# Revit family: Haworth_BuzziNordic_ST100_LoungeChair
name_source: partatom
category: Furniture
revit_build: Autodesk Revit 2018 (Build: 20170223_1515(x64)
units: mm (PartAtom-declared; Revit-internal decimal feet)

## family parameters
Always vertical = Yes
Cut with Voids When Loaded = No
Room Calculation Point = No
Shared = No
Work Plane-Based = No

## types (2) — shared parameters
Actual Depth = 30.71 "
Actual Height = 31.89 "
Assembly Code = E2020200
Manufacturer = Haworth
Model = HCBZ-N1L1
Note = Verify Final Dim. w/ Haworth
Revision = 1
Seat Height = 16.54 "
URL = http://www.haworth.com
URL - Product = https://www.haworth.com
Warranty = http://www.haworth.com

## per-type parameters (varying)
| type | Actual Width | Back Support Width | Description | Seat Width | Spindle Offset | Wide |
| HCBZ-N1L1 - Lounge Chair | 28.15 " | 23.4 " | Haworth BuzziNordic Lounge Chair | 22.05 " | 3.9 " | No |
| HCBZ-N1L1-W - Wide Lounge Chair | 32.68 " | 27.93 " | Haworth BuzziNordic Lounge Chair Wide | 27.95 " | 4.65 " | Yes |

## geometry (parser evidence)
native form markers: Sweep x8
no freeform markers — native parametric forms only
